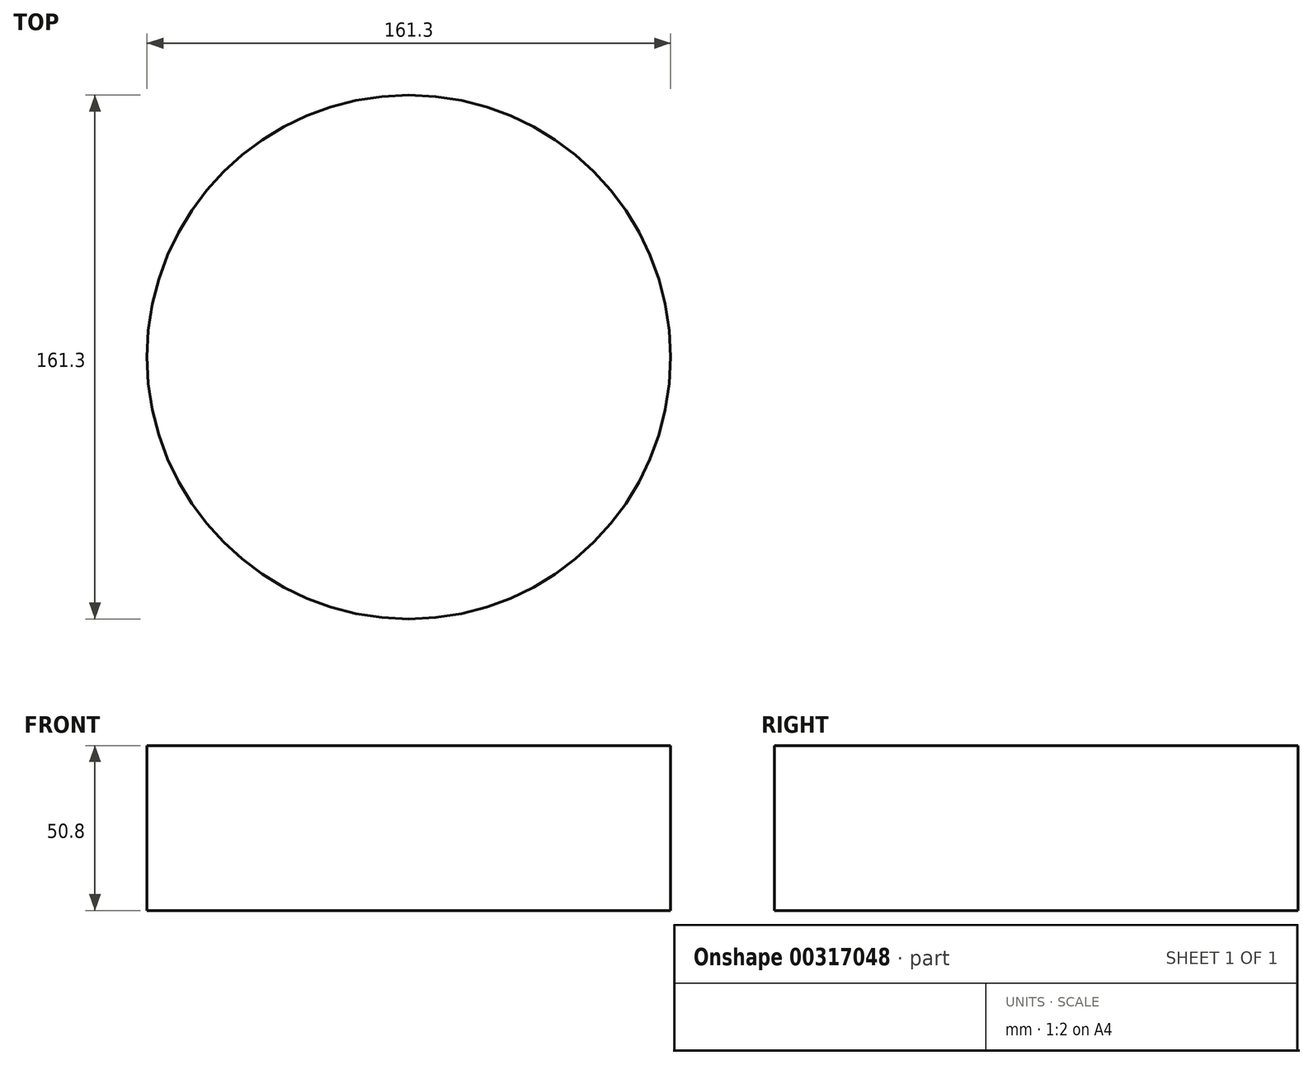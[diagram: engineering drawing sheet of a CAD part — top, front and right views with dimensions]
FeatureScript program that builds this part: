
annotation { "Feature Type Name" : "Feature", "Feature Type Description" : "" }
export const myFeature = defineFeature(function(context is Context, id is Id, definition is map)
    precondition{}
    {
        {
            var Q0;
            Q0=qCreatedBy(makeId("Top.planeOp"),FACE);
            var sketch = newSketch(context, id + "F0", { "sketchPlane" : qUnion([Q0])});
            skCircle(sketch, "E0", {"center": v(0, 0) * mm, "radius": 80.65 * mm});
            skSolve(sketch);
        }
        {
            var Q0;
            Q0 = qSketchRegion(id + "F0", true);
            extrude(context, id + "F1", {"entities" : qUnion([Q0]), "depth" : 50.8 * mm, "symmetric" : true});
        }
    });
